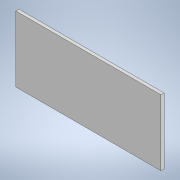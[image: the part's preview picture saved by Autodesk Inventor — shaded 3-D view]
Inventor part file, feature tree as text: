
AUTODESK INVENTOR PART (.ipt)
format: ipt  version: 2021 (Build 250183000, 183)  size: 89,088 bytes
history: native  units: mm
features: extrude x1, sketch x1
ambient origin geometry x8: Origin, YZ Plane, XZ Plane, XY Plane, X Axis, Y Axis, Z Axis, Center Point
bodies: Solid1 (feature_tree)
feature tree (2):
  extrude  "Extrusion1"  Depth=42.5mm
  sketch  "Sketch1"  dims[d0=93.6mm d1=42.5mm d2=2.0mm d3=0.0mm]
